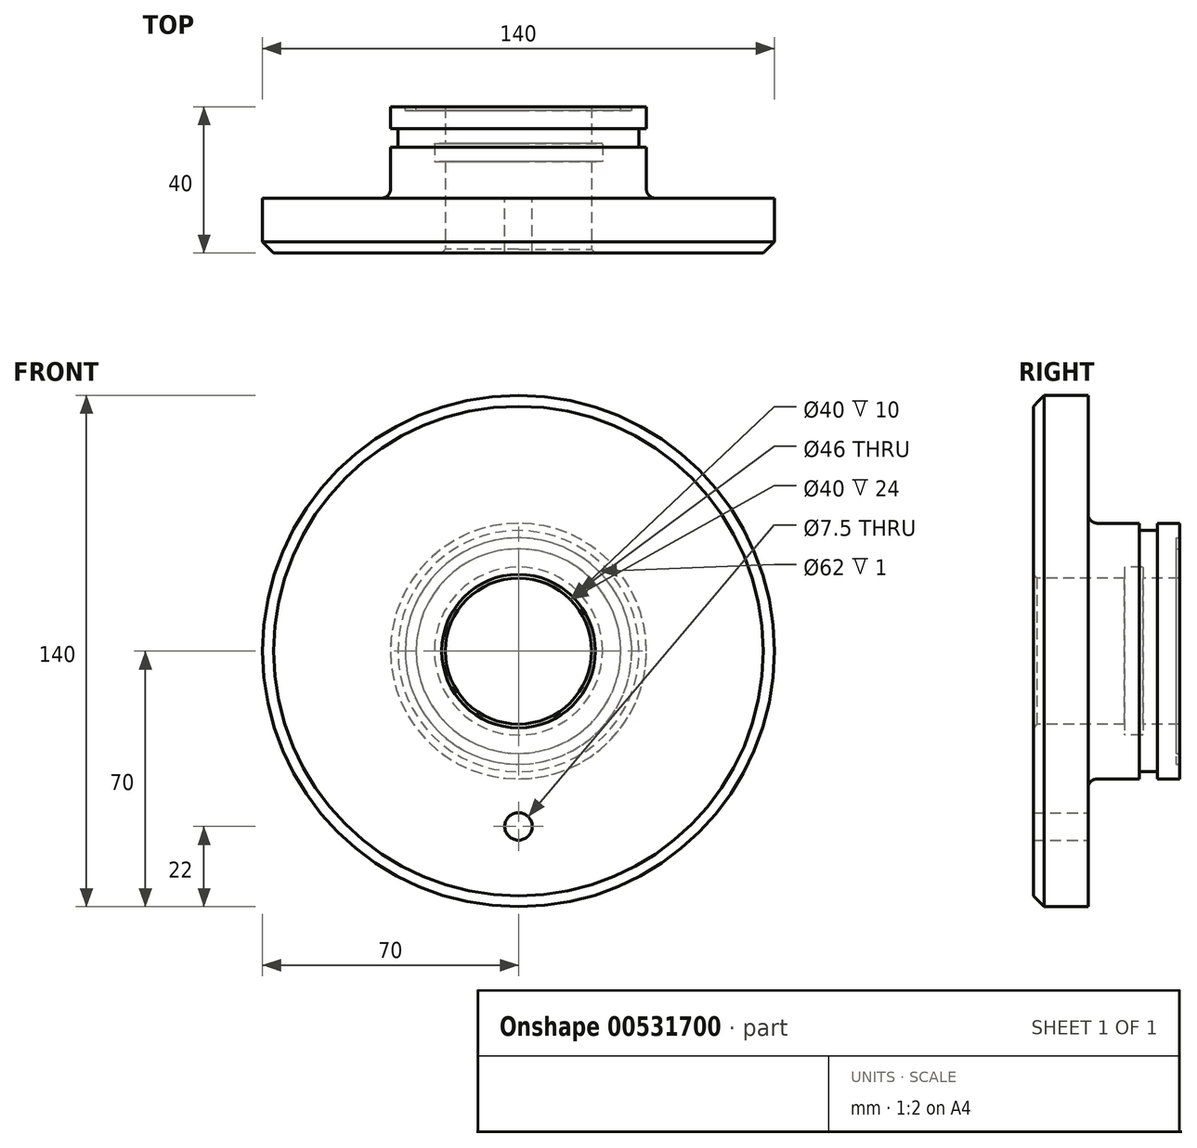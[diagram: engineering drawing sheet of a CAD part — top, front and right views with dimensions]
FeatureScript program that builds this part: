
annotation { "Feature Type Name" : "Feature", "Feature Type Description" : "" }
export const myFeature = defineFeature(function(context is Context, id is Id, definition is map)
    precondition{}
    {
        {
            var Q0;
            Q0=qCreatedBy(makeId("Top.planeOp"),FACE);
            var sketch = newSketch(context, id + "F0", { "sketchPlane" : qUnion([Q0])});
            skLineSegment(sketch, "E0", {"start": v(0, 0) * mm, "end": v(0, 97.97) * mm, "construction": true});
            skLineSegment(sketch, "E1", {"start": v(35, 15) * mm, "end": v(70, 15) * mm});
            skLineSegment(sketch, "E2", {"start": v(70, 15) * mm, "end": v(70, 0) * mm});
            skLineSegment(sketch, "E3", {"start": v(70, 0) * mm, "end": v(20, 0) * mm});
            skLineSegment(sketch, "E4", {"start": v(20, 0) * mm, "end": v(20, 25) * mm});
            skLineSegment(sketch, "E5", {"start": v(87.34, 0) * mm, "end": v(0, 0) * mm, "construction": true});
            skLineSegment(sketch, "E6", {"start": v(23, 25) * mm, "end": v(20, 25) * mm});
            skLineSegment(sketch, "E7", {"start": v(23, 30) * mm, "end": v(23, 25) * mm});
            skLineSegment(sketch, "E8", {"start": v(23, 30) * mm, "end": v(20, 30) * mm});
            skLineSegment(sketch, "E9", {"start": v(20, 30) * mm, "end": v(20, 40) * mm});
            skLineSegment(sketch, "E10", {"start": v(20, 40) * mm, "end": v(35, 40) * mm});
            skLineSegment(sketch, "E11", {"start": v(35, 15) * mm, "end": v(35, 40) * mm});
            skSolve(sketch);
        }
        {
            var Q0;
            Q0=makeQuery(id+"F0.imprint","IMPRINT",FACE,{"disambiguationData":[TD([[makeQuery(id+"F0.imprint","IMPRINT",EDGE,{"derivedFrom":sQuery(id+"F0.wireOp",EDGE,"E1")}),-1.0]])]});
            var Q1;
            Q1=sQuery(id+"F0.wireOp",EDGE,"E0");
            revolve(context, id + "F1", {"entities" : qUnion([Q0]), "axis" : qUnion([Q1]), "revolveType" : RevolveType.FULL});
        }
        {
            var Q0;
            Q0=makeQuery(id+"F1.opRevolve","SWEPT_EDGE",EDGE,{"disambiguationData":[OSD([sQuery(id+"F0.wireOp",EDGE,"E1"),sQuery(id+"F0.wireOp",EDGE,"E11")])]});
            fillet(context, id + "F2", {"entities" : qUnion([Q0]), "radius" : 2.5 * mm, "tangentPropagation" : true, "defaultsChanged" : false, "vertexSettings" : [], "allowEdgeOverflow" : false});
        }
        {
            var Q0;
            Q0=makeQuery(id+"F1.opRevolve","SWEPT_EDGE",EDGE,{"disambiguationData":[OSD([sQuery(id+"F0.wireOp",EDGE,"E7"),sQuery(id+"F0.wireOp",EDGE,"E8")])]});
            var Q1;
            Q1=makeQuery(id+"F1.opRevolve","SWEPT_EDGE",EDGE,{"disambiguationData":[OSD([sQuery(id+"F0.wireOp",EDGE,"E6"),sQuery(id+"F0.wireOp",EDGE,"E7")])]});
            fillet(context, id + "F3", {"entities" : qUnion([Q0, Q1]), "radius" : .25 * mm, "tangentPropagation" : true, "allowEdgeOverflow" : false});
        }
        {
            var Q0;
            Q0=makeQuery(id+"F1.opRevolve","SWEPT_EDGE",EDGE,{"disambiguationData":[OSD([sQuery(id+"F0.wireOp",EDGE,"E3"),sQuery(id+"F0.wireOp",EDGE,"E4")])]});
            chamfer(context, id + "F4", {"entities" : qUnion([Q0]), "width" : 1 * mm, "tangentPropagation" : true});
        }
        {
            var Q0;
            Q0=makeQuery(id+"F1.opRevolve","SWEPT_EDGE",EDGE,{"disambiguationData":[OSD([sQuery(id+"F0.wireOp",EDGE,"E2"),sQuery(id+"F0.wireOp",EDGE,"E3")])]});
            chamfer(context, id + "F5", {"entities" : qUnion([Q0]), "width" : 3 * mm, "tangentPropagation" : true});
        }
        {
            var Q0;
            Q0=makeQuery(id+"F1.opRevolve","SWEPT_FACE",FACE,{"disambiguationData":[OSD([sQuery(id+"F0.wireOp",EDGE,"E1")])]});
            var sketch = newSketch(context, id + "F6", { "sketchPlane" : qUnion([Q0])});
            skPoint(sketch, "E12", {"position": v(0, -48) * mm});
            skCircle(sketch, "E13", {"center": v(0, 0) * mm, "radius": 48 * mm, "construction": true});
            skSolve(sketch);
        }
        {
            var Q0;
            Q0=sQuery(id+"F6.wireOp",VERTEX,"E12");
            var Q1;
            Q1=makeQuery(id+"F1.opRevolve","SWEPT_BODY",BODY,{"disambiguationData":[OSD([sQuery(id+"F0.wireOp",EDGE,"E1"),sQuery(id+"F0.wireOp",EDGE,"E2"),sQuery(id+"F0.wireOp",EDGE,"E3"),sQuery(id+"F0.wireOp",EDGE,"E4"),sQuery(id+"F0.wireOp",EDGE,"E6"),sQuery(id+"F0.wireOp",EDGE,"E7"),sQuery(id+"F0.wireOp",EDGE,"E8"),sQuery(id+"F0.wireOp",EDGE,"E9"),sQuery(id+"F0.wireOp",EDGE,"E10"),sQuery(id+"F0.wireOp",EDGE,"E11")])]});
            hole(context, id + "F7", {"style" : HoleStyle.SIMPLE, "endStyle" : HoleEndStyle.THROUGH, "holeDiameter" : 7.5 * mm, "isTappedThrough" : true, "tappedDepth" : 12 * mm, "tapClearance" : 3, "locations" : qUnion([Q0]), "scope" : qUnion([Q1])});
        }
        {
            var Q0;
            Q0=qCreatedBy(makeId("Right.planeOp"),FACE);
            var sketch = newSketch(context, id + "F8", { "sketchPlane" : qUnion([Q0])});
            skLineSegment(sketch, "E14", {"start": v(29, 45.38) * mm, "end": v(29, 33) * mm});
            skLineSegment(sketch, "E15", {"start": v(29, 33) * mm, "end": v(34, 33) * mm});
            skLineSegment(sketch, "E16", {"start": v(34, 33) * mm, "end": v(34, 45.38) * mm});
            skLineSegment(sketch, "E17", {"start": v(34, 45.38) * mm, "end": v(29, 45.38) * mm});
            skLineSegment(sketch, "E18", {"start": v(0, 0) * mm, "end": v(67.67, 0) * mm, "construction": true});
            skSolve(sketch);
        }
        {
            var Q0;
            Q0 = qSketchRegion(id + "F8", true);
            var Q1;
            Q1=sQuery(id+"F8.wireOp",EDGE,"E18");
            revolve(context, id + "F9", {"operationType" : NewBodyOperationType.REMOVE, "entities" : qUnion([Q0]), "axis" : qUnion([Q1]), "revolveType" : RevolveType.FULL, "oppositeDirection" : true});
        }
        {
            var Q0;
            Q0=qCreatedBy(makeId("Right.planeOp"),FACE);
            var sketch = newSketch(context, id + "F10", { "sketchPlane" : qUnion([Q0])});
            skLineSegment(sketch, "E19", {"start": v(0, 0) * mm, "end": v(52.79, 0) * mm, "construction": true});
            skLineSegment(sketch, "E20", {"start": v(42.98, 31) * mm, "end": v(39, 31) * mm});
            skLineSegment(sketch, "E21", {"start": v(39, 31) * mm, "end": v(39, 28) * mm});
            skLineSegment(sketch, "E22", {"start": v(39, 28) * mm, "end": v(42.98, 28) * mm});
            skLineSegment(sketch, "E23", {"start": v(42.98, 28) * mm, "end": v(42.98, 31) * mm});
            skSolve(sketch);
        }
        {
            var Q0;
            Q0 = qSketchRegion(id + "F10", true);
            var Q1;
            Q1=sQuery(id+"F10.wireOp",EDGE,"E19");
            revolve(context, id + "F11", {"operationType" : NewBodyOperationType.REMOVE, "entities" : qUnion([Q0]), "axis" : qUnion([Q1]), "revolveType" : RevolveType.FULL, "oppositeDirection" : true});
        }
    });
